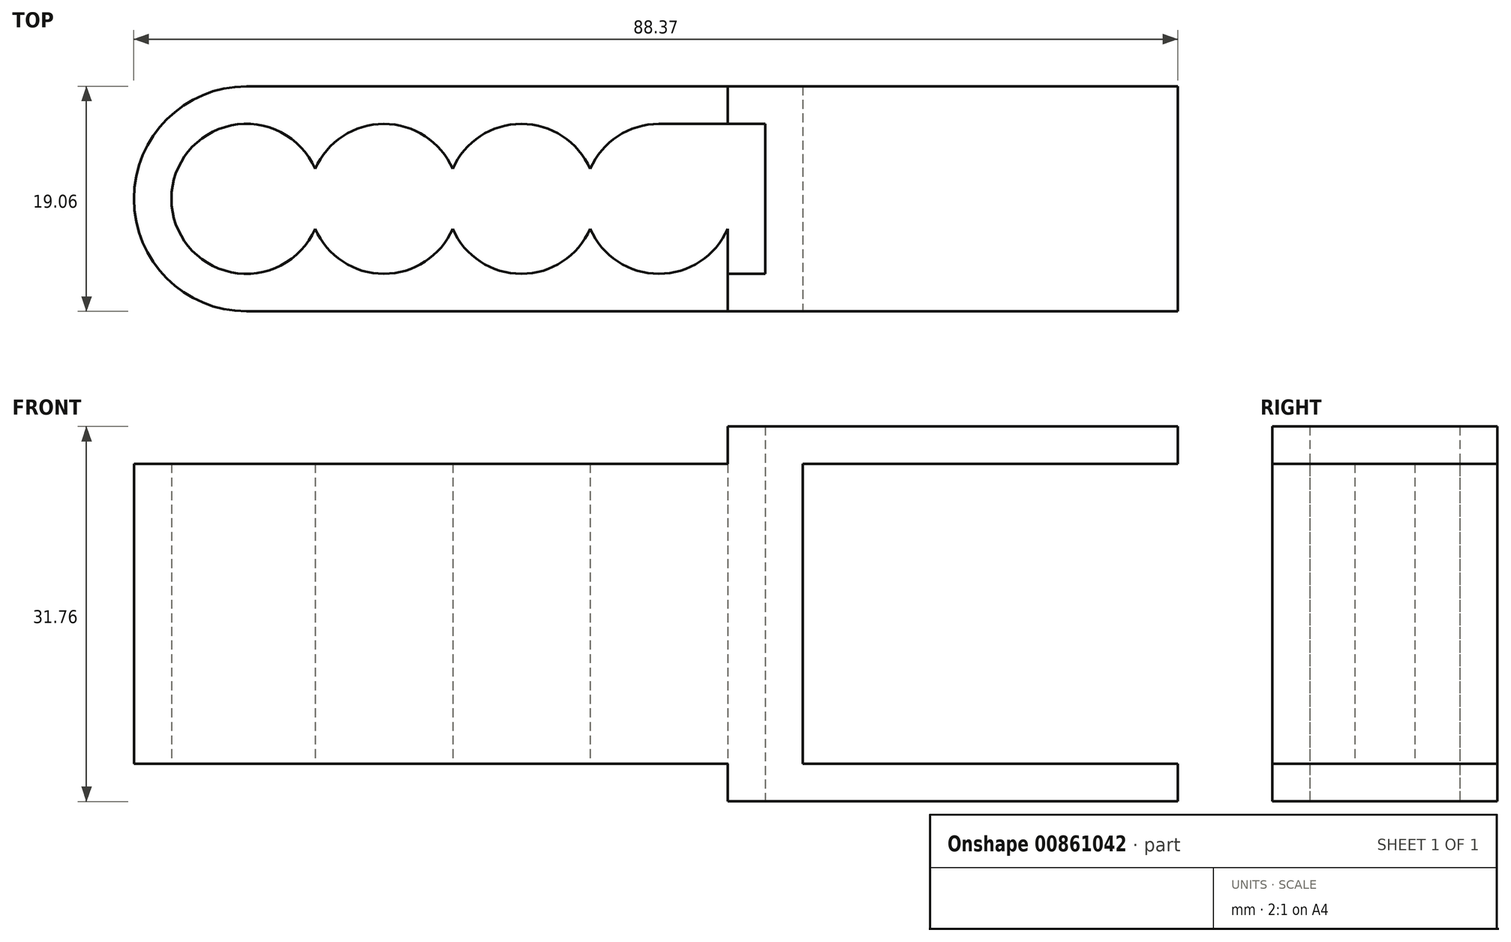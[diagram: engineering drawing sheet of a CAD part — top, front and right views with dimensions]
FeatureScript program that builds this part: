
annotation { "Feature Type Name" : "Feature", "Feature Type Description" : "" }
export const myFeature = defineFeature(function(context is Context, id is Id, definition is map)
    precondition{}
    {
        {
            var Q0;
            Q0=qCreatedBy(makeId("Top.planeOp"),FACE);
            var sketch = newSketch(context, id + "F0", { "sketchPlane" : qUnion([Q0])});
            skArc(sketch, "E0", {"start": v(0, 9.53) * mm, "mid": v(-9.53, 0) * mm, "end": v(0, -9.53) * mm});
            skArc(sketch, "E1", {"start": v(5.82, 2.54) * mm, "mid": v(-6.35, 0) * mm, "end": v(5.82, -2.54) * mm});
            skLineSegment(sketch, "E2", {"start": v(0, 9.52) * mm, "end": v(40.74, 9.52) * mm});
            skLineSegment(sketch, "E3", {"start": v(0, -9.53) * mm, "end": v(40.74, -9.52) * mm});
            skLineSegment(sketch, "E4", {"start": v(0, -6.35) * mm, "end": v(40.74, -6.35) * mm});
            skLineSegment(sketch, "E5", {"start": v(0, 6.35) * mm, "end": v(40.74, 6.35) * mm});
            skArc(sketch, "E6.MirrorCS", {"start": v(5.82, 2.54) * mm, "mid": v(11.64, 6.35) * mm, "end": v(17.46, 2.54) * mm});
            skArc(sketch, "E7.trimOffspring", {"start": v(17.46, -2.54) * mm, "mid": v(11.64, -6.35) * mm, "end": v(5.82, -2.54) * mm});
            skArc(sketch, "E8.MirrorCS", {"start": v(29.1, 2.54) * mm, "mid": v(23.28, 6.35) * mm, "end": v(17.46, 2.54) * mm});
            skArc(sketch, "E9.MirrorCS", {"start": v(17.46, -2.54) * mm, "mid": v(23.28, -6.35) * mm, "end": v(29.1, -2.54) * mm});
            skArc(sketch, "E10.MirrorCS", {"start": v(29.1, 2.54) * mm, "mid": v(34.92, 6.35) * mm, "end": v(40.74, 2.54) * mm});
            skLineSegment(sketch, "E11", {"start": v(40.74, 2.54) * mm, "end": v(40.74, 9.52) * mm});
            skLineSegment(sketch, "E12", {"start": v(40.74, 9.52) * mm, "end": v(40.74, 2.54) * mm});
            skArc(sketch, "E13.trimOffspring", {"start": v(40.74, -2.54) * mm, "mid": v(34.92, -6.35) * mm, "end": v(29.1, -2.54) * mm});
            skLineSegment(sketch, "E14.trimOffspring", {"start": v(40.74, -2.54) * mm, "end": v(40.74, -9.52) * mm});
            skLineSegment(sketch, "E15", {"start": v(40.74, 9.52) * mm, "end": v(78.84, 9.53) * mm});
            skLineSegment(sketch, "E16", {"start": v(78.84, -9.52) * mm, "end": v(40.74, -9.52) * mm});
            skLineSegment(sketch, "E17", {"start": v(40.74, 6.35) * mm, "end": v(78.84, 6.35) * mm});
            skLineSegment(sketch, "E18", {"start": v(40.74, -6.35) * mm, "end": v(78.84, -6.35) * mm});
            skPoint(sketch, "E19", {"position": v(-9.53, 0) * mm});
            skLineSegment(sketch, "E20", {"start": v(78.84, 9.53) * mm, "end": v(78.84, -9.53) * mm});
            skLineSegment(sketch, "E21", {"start": v(75.66, 9.52) * mm, "end": v(75.66, -9.52) * mm});
            skLineSegment(sketch, "E22", {"start": v(43.91, 9.52) * mm, "end": v(43.91, -9.52) * mm});
            skLineSegment(sketch, "E23", {"start": v(47.09, 9.52) * mm, "end": v(47.09, -9.52) * mm});
            skSolve(sketch);
        }
        {
            var Q0;
            Q0=makeQuery(id+"F0.imprint","IMPRINT",FACE,{"disambiguationData":[TD([[makeQuery(id+"F0.imprint","IMPRINT",EDGE,{"derivedFrom":sQuery(id+"F0.wireOp",EDGE,"E0")}),1.0]])]});
            var Q1;
            {var subQ0=sQuery(id+"F0.wireOp",EDGE,"E6.MirrorCS");var subQ1=sQuery(id+"F0.wireOp",EDGE,"E1");var subQ2=makeQuery(id+"F0.imprint","INTERSECT",VERTEX,{"derivedFrom":[subQ1,subQ0]});Q1=makeQuery(id+"F0.imprint","IMPRINT",FACE,{"disambiguationData":[TD([[makeQuery(id+"F0.imprint","IMPRINT",EDGE,{"disambiguationData":[TD([[subQ2,-1.0]])],"derivedFrom":subQ1}),-1.0]])]});}
            var Q2;
            {var subQ0=sQuery(id+"F0.wireOp",EDGE,"E6.MirrorCS");var subQ1=sQuery(id+"F0.wireOp",EDGE,"E5");var subQ2=makeQuery(id+"F0.imprint","INTERSECT",VERTEX,{"derivedFrom":[subQ1,subQ0]});Q2=makeQuery(id+"F0.imprint","IMPRINT",FACE,{"disambiguationData":[TD([[makeQuery(id+"F0.imprint","IMPRINT",EDGE,{"disambiguationData":[TD([[subQ2,-1.0]])],"derivedFrom":subQ1}),-1.0]])]});}
            var Q3;
            {var subQ0=sQuery(id+"F0.wireOp",EDGE,"E8.MirrorCS");var subQ1=sQuery(id+"F0.wireOp",EDGE,"E5");var subQ2=makeQuery(id+"F0.imprint","INTERSECT",VERTEX,{"derivedFrom":[subQ1,subQ0]});Q3=makeQuery(id+"F0.imprint","IMPRINT",FACE,{"disambiguationData":[TD([[makeQuery(id+"F0.imprint","IMPRINT",EDGE,{"disambiguationData":[TD([[subQ2,-1.0]])],"derivedFrom":subQ1}),-1.0]])]});}
            var Q4;
            {var subQ0=sQuery(id+"F0.wireOp",EDGE,"E12");var subQ1=sQuery(id+"F0.wireOp",EDGE,"E5");var subQ2=makeQuery(id+"F0.imprint","INTERSECT",VERTEX,{"derivedFrom":[subQ1,subQ0]});Q4=makeQuery(id+"F0.imprint","IMPRINT",FACE,{"disambiguationData":[TD([[makeQuery(id+"F0.imprint","IMPRINT",EDGE,{"disambiguationData":[TD([[subQ2,1.0]])],"derivedFrom":subQ1}),-1.0]])]});}
            var Q5;
            {var subQ0=sQuery(id+"F0.wireOp",EDGE,"E9.MirrorCS");var subQ1=sQuery(id+"F0.wireOp",EDGE,"E4");var subQ2=makeQuery(id+"F0.imprint","INTERSECT",VERTEX,{"derivedFrom":[subQ1,subQ0]});Q5=makeQuery(id+"F0.imprint","IMPRINT",FACE,{"disambiguationData":[TD([[makeQuery(id+"F0.imprint","IMPRINT",EDGE,{"disambiguationData":[TD([[subQ2,-1.0]])],"derivedFrom":subQ1}),1.0]])]});}
            var Q6;
            {var subQ0=sQuery(id+"F0.wireOp",EDGE,"E14.trimOffspring");var subQ1=sQuery(id+"F0.wireOp",EDGE,"E4");var subQ2=makeQuery(id+"F0.imprint","INTERSECT",VERTEX,{"derivedFrom":[subQ1,subQ0]});Q6=makeQuery(id+"F0.imprint","IMPRINT",FACE,{"disambiguationData":[TD([[makeQuery(id+"F0.imprint","IMPRINT",EDGE,{"disambiguationData":[TD([[subQ2,1.0]])],"derivedFrom":subQ1}),1.0]])]});}
            var Q7;
            {var subQ0=sQuery(id+"F0.wireOp",EDGE,"E7.trimOffspring");var subQ1=sQuery(id+"F0.wireOp",EDGE,"E4");var subQ2=makeQuery(id+"F0.imprint","INTERSECT",VERTEX,{"derivedFrom":[subQ1,subQ0]});Q7=makeQuery(id+"F0.imprint","IMPRINT",FACE,{"disambiguationData":[TD([[makeQuery(id+"F0.imprint","IMPRINT",EDGE,{"disambiguationData":[TD([[subQ2,-1.0]])],"derivedFrom":subQ1}),1.0]])]});}
            var Q8;
            {var subQ0=sQuery(id+"F0.wireOp",EDGE,"E7.trimOffspring");var subQ1=sQuery(id+"F0.wireOp",EDGE,"E1");var subQ2=makeQuery(id+"F0.imprint","INTERSECT",VERTEX,{"derivedFrom":[subQ1,subQ0]});Q8=makeQuery(id+"F0.imprint","IMPRINT",FACE,{"disambiguationData":[TD([[makeQuery(id+"F0.imprint","IMPRINT",EDGE,{"disambiguationData":[TD([[subQ2,1.0]])],"derivedFrom":subQ1}),-1.0]])]});}
            extrude(context, id + "F1", {"entities" : qUnion([Q0, Q1, Q2, Q3, Q4, Q5, Q6, Q7, Q8]), "endBound" : BoundingType.SYMMETRIC, "depth" : 25.4 * mm, "offsetDistance" : 25.4 * mm});
        }
        {
            var Q0;
            {var subQ0=sQuery(id+"F0.wireOp",EDGE,"E22");var subQ1=sQuery(id+"F0.wireOp",EDGE,"E17");var subQ2=makeQuery(id+"F0.imprint","INTERSECT",VERTEX,{"derivedFrom":[subQ1,subQ0]});Q0=makeQuery(id+"F0.imprint","IMPRINT",FACE,{"disambiguationData":[TD([[makeQuery(id+"F0.imprint","IMPRINT",EDGE,{"disambiguationData":[TD([[subQ2,-1.0]])],"derivedFrom":subQ1}),-1.0]])]});}
            var Q1;
            {var subQ0=sQuery(id+"F0.wireOp",EDGE,"E23");var subQ1=sQuery(id+"F0.wireOp",EDGE,"E17");var subQ2=makeQuery(id+"F0.imprint","INTERSECT",VERTEX,{"derivedFrom":[subQ1,subQ0]});Q1=makeQuery(id+"F0.imprint","IMPRINT",FACE,{"disambiguationData":[TD([[makeQuery(id+"F0.imprint","IMPRINT",EDGE,{"disambiguationData":[TD([[subQ2,-1.0]])],"derivedFrom":subQ1}),-1.0]])]});}
            var Q2;
            {var subQ0=sQuery(id+"F0.wireOp",EDGE,"E20");var subQ1=sQuery(id+"F0.wireOp",EDGE,"E17");var subQ2=makeQuery(id+"F0.imprint","INTERSECT",VERTEX,{"derivedFrom":[subQ1,subQ0]});Q2=makeQuery(id+"F0.imprint","IMPRINT",FACE,{"disambiguationData":[TD([[makeQuery(id+"F0.imprint","IMPRINT",EDGE,{"disambiguationData":[TD([[subQ2,1.0]])],"derivedFrom":subQ1}),-1.0]])]});}
            var Q3;
            {var subQ0=sQuery(id+"F0.wireOp",EDGE,"E22");var subQ1=sQuery(id+"F0.wireOp",EDGE,"E15");var subQ2=makeQuery(id+"F0.imprint","INTERSECT",VERTEX,{"derivedFrom":[subQ1,subQ0]});Q3=makeQuery(id+"F0.imprint","IMPRINT",FACE,{"disambiguationData":[TD([[makeQuery(id+"F0.imprint","IMPRINT",EDGE,{"disambiguationData":[TD([[subQ2,-1.0]])],"derivedFrom":subQ1}),-1.0]])]});}
            var Q4;
            {var subQ0=sQuery(id+"F0.wireOp",EDGE,"E15");var subQ5=sQuery(id+"F0.wireOp",EDGE,"E22");var subQ6=makeQuery(id+"F0.imprint","INTERSECT",VERTEX,{"derivedFrom":[subQ0,subQ5]});Q4=makeQuery(id+"F0.imprint","IMPRINT",FACE,{"disambiguationData":[TD([[makeQuery(id+"F0.imprint","IMPRINT",EDGE,{"disambiguationData":[TD([[subQ6,-1.0]])],"derivedFrom":subQ5}),-1.0]])]});}
            var Q5;
            {var subQ0=sQuery(id+"F0.wireOp",EDGE,"E21");var subQ1=sQuery(id+"F0.wireOp",EDGE,"E15");var subQ2=makeQuery(id+"F0.imprint","INTERSECT",VERTEX,{"derivedFrom":[subQ1,subQ0]});Q5=makeQuery(id+"F0.imprint","IMPRINT",FACE,{"disambiguationData":[TD([[makeQuery(id+"F0.imprint","IMPRINT",EDGE,{"disambiguationData":[TD([[subQ2,1.0]])],"derivedFrom":subQ1}),-1.0]])]});}
            var Q6;
            {var subQ0=sQuery(id+"F0.wireOp",EDGE,"E20");var subQ1=sQuery(id+"F0.wireOp",EDGE,"E15");var subQ2=makeQuery(id+"F0.imprint","INTERSECT",VERTEX,{"derivedFrom":[subQ1,subQ0]});Q6=makeQuery(id+"F0.imprint","IMPRINT",FACE,{"disambiguationData":[TD([[makeQuery(id+"F0.imprint","IMPRINT",EDGE,{"disambiguationData":[TD([[subQ2,1.0]])],"derivedFrom":subQ1}),-1.0]])]});}
            var Q7;
            {var subQ0=sQuery(id+"F0.wireOp",EDGE,"E16");var subQ5=sQuery(id+"F0.wireOp",EDGE,"E22");var subQ6=makeQuery(id+"F0.imprint","INTERSECT",VERTEX,{"derivedFrom":[subQ0,subQ5]});Q7=makeQuery(id+"F0.imprint","IMPRINT",FACE,{"disambiguationData":[TD([[makeQuery(id+"F0.imprint","IMPRINT",EDGE,{"disambiguationData":[TD([[subQ6,1.0]])],"derivedFrom":subQ5}),-1.0]])]});}
            var Q8;
            {var subQ0=sQuery(id+"F0.wireOp",EDGE,"E22");var subQ1=sQuery(id+"F0.wireOp",EDGE,"E16");var subQ2=makeQuery(id+"F0.imprint","INTERSECT",VERTEX,{"derivedFrom":[subQ1,subQ0]});Q8=makeQuery(id+"F0.imprint","IMPRINT",FACE,{"disambiguationData":[TD([[makeQuery(id+"F0.imprint","IMPRINT",EDGE,{"disambiguationData":[TD([[subQ2,1.0]])],"derivedFrom":subQ1}),-1.0]])]});}
            var Q9;
            {var subQ0=sQuery(id+"F0.wireOp",EDGE,"E21");var subQ1=sQuery(id+"F0.wireOp",EDGE,"E16");var subQ2=makeQuery(id+"F0.imprint","INTERSECT",VERTEX,{"derivedFrom":[subQ1,subQ0]});Q9=makeQuery(id+"F0.imprint","IMPRINT",FACE,{"disambiguationData":[TD([[makeQuery(id+"F0.imprint","IMPRINT",EDGE,{"disambiguationData":[TD([[subQ2,-1.0]])],"derivedFrom":subQ1}),-1.0]])]});}
            var Q10;
            {var subQ0=sQuery(id+"F0.wireOp",EDGE,"E20");var subQ1=sQuery(id+"F0.wireOp",EDGE,"E16");var subQ2=makeQuery(id+"F0.imprint","INTERSECT",VERTEX,{"derivedFrom":[subQ1,subQ0]});Q10=makeQuery(id+"F0.imprint","IMPRINT",FACE,{"disambiguationData":[TD([[makeQuery(id+"F0.imprint","IMPRINT",EDGE,{"disambiguationData":[TD([[subQ2,-1.0]])],"derivedFrom":subQ1}),-1.0]])]});}
            extrude(context, id + "F2", {"entities" : qUnion([Q0, Q1, Q2, Q3, Q4, Q5, Q6, Q7, Q8, Q9, Q10]), "operationType" : NewBodyOperationType.ADD, "endBound" : BoundingType.SYMMETRIC, "depth" : 31.75 * mm, "offsetDistance" : 25.4 * mm});
        }
        {
            var Q0;
            Q0=makeQuery(id+"F2.opExtrude","SWEPT_FACE",FACE,{"disambiguationData":[OSD([sQuery(id+"F0.wireOp",EDGE,"E20")])]});
            shell(context, id + "F3", {"entities" : qUnion([Q0]), "thickness" : 3.17 * mm});
        }
        {
            var Q0;
            Q0=makeQuery(id+"F2.opExtrude","SWEPT_FACE",FACE,{"disambiguationData":[OSD([sQuery(id+"F0.wireOp",EDGE,"E20")])]});
            var sketch = newSketch(context, id + "F4", { "sketchPlane" : qUnion([Q0])});
            skLineSegment(sketch, "E24.bottom", {"start": v(6.35, 12.7) * mm, "end": v(9.52, 12.7) * mm});
            skLineSegment(sketch, "E24.top", {"start": v(6.35, -12.7) * mm, "end": v(9.52, -12.7) * mm});
            skLineSegment(sketch, "E24.left", {"start": v(6.35, 12.7) * mm, "end": v(6.35, -12.7) * mm});
            skLineSegment(sketch, "E24.right", {"start": v(9.52, 12.7) * mm, "end": v(9.52, -12.7) * mm});
            skLineSegment(sketch, "E25.bottom", {"start": v(-6.35, 12.7) * mm, "end": v(-9.53, 12.7) * mm});
            skLineSegment(sketch, "E25.top", {"start": v(-6.35, -12.7) * mm, "end": v(-9.53, -12.7) * mm});
            skLineSegment(sketch, "E25.left", {"start": v(-6.35, 12.7) * mm, "end": v(-6.35, -12.7) * mm});
            skLineSegment(sketch, "E25.right", {"start": v(-9.53, 12.7) * mm, "end": v(-9.53, -12.7) * mm});
            skSolve(sketch);
        }
        {
            var Q0;
            Q0 = qSketchRegion(id + "F4", true);
            var Q1;
            Q1=makeQuery(id+"F3.opShell","OFFSET_FACE",FACE,{"disambiguationData":[OSD([sQuery(id+"F0.wireOp",EDGE,"E22")])]});
            extrude(context, id + "F5", {"entities" : qUnion([Q0]), "operationType" : NewBodyOperationType.REMOVE, "endBound" : BoundingType.UP_TO_SURFACE, "oppositeDirection" : true, "depth" : 34.1 * mm, "endBoundEntityFace" : qUnion([Q1]), "offsetDistance" : 25.4 * mm});
        }
    });
